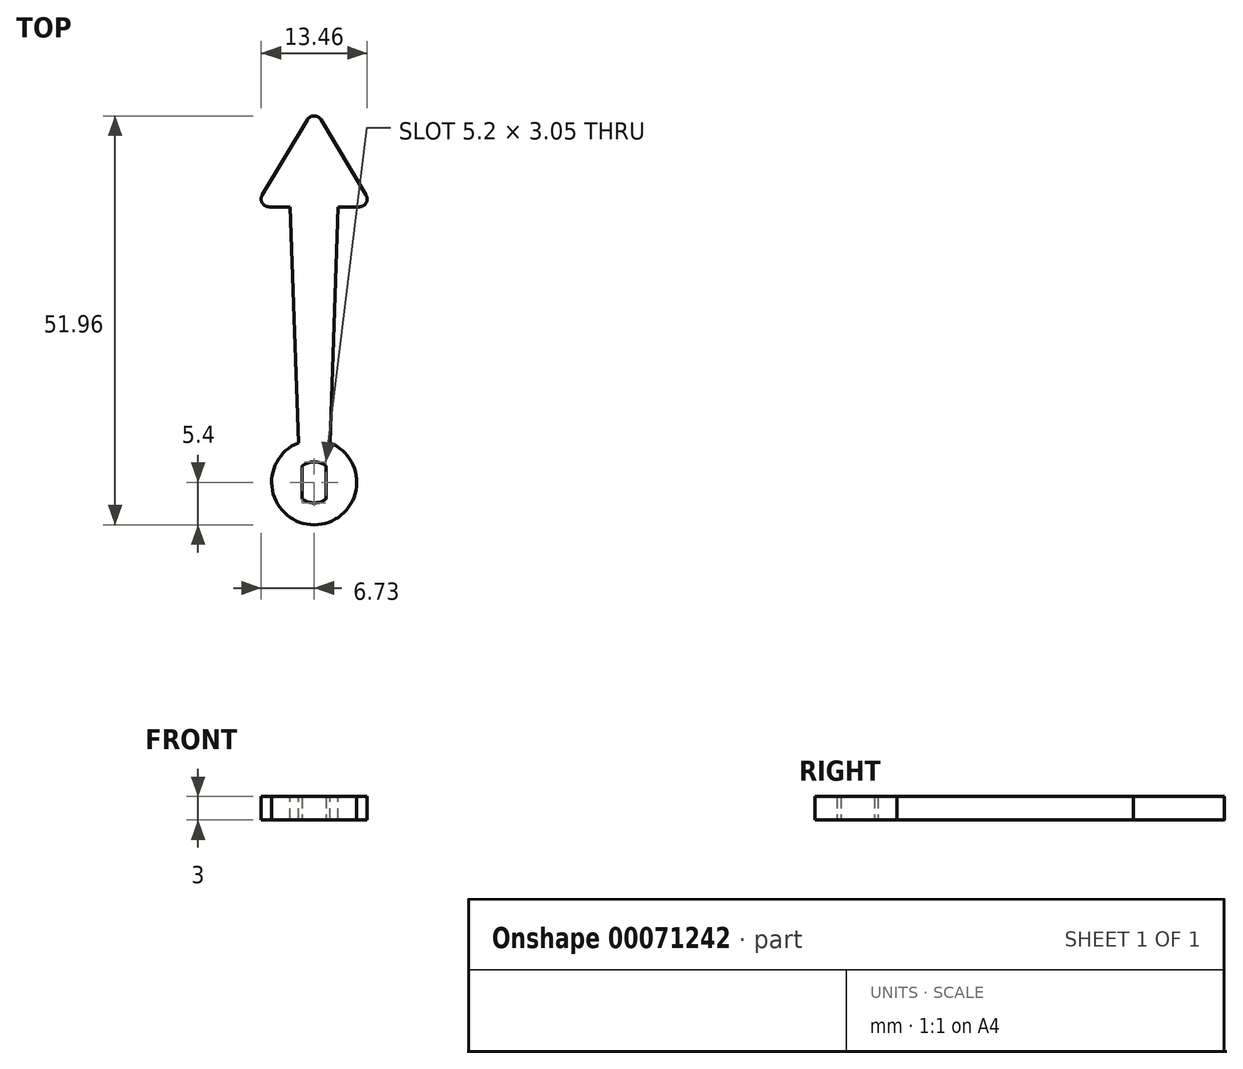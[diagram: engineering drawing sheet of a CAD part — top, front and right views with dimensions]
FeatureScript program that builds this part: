
annotation { "Feature Type Name" : "Feature", "Feature Type Description" : "" }
export const myFeature = defineFeature(function(context is Context, id is Id, definition is map)
    precondition{}
    {
        {
            var Q0;
            Q0=qCreatedBy(makeId("Top.planeOp"),FACE);
            var sketch = newSketch(context, id + "F0", { "sketchPlane" : qUnion([Q0])});
            skCircle(sketch, "E0", {"center": v(0, 0) * mm, "radius": 5.4 * mm});
            skCircle(sketch, "E1", {"center": v(0, 0) * mm, "radius": 2.6 * mm});
            skLineSegment(sketch, "E2", {"start": v(-1.52, 2.1) * mm, "end": v(-1.52, -2.1) * mm});
            skLineSegment(sketch, "E3", {"start": v(1.53, 2.1) * mm, "end": v(1.53, -2.1) * mm});
            skSolve(sketch);
        }
        {
            var Q0;
            Q0=makeQuery(id+"F0.imprint","IMPRINT",FACE,{"disambiguationData":[TD([[makeQuery(id+"F0.imprint","IMPRINT",EDGE,{"derivedFrom":sQuery(id+"F0.wireOp",EDGE,"E0")}),1.0]])]});
            var Q1;
            {var subQ0=sQuery(id+"F0.wireOp",EDGE,"E2");Q1=makeQuery(id+"F0.imprint","IMPRINT",FACE,{"disambiguationData":[TD([[makeQuery(id+"F0.imprint","IMPRINT",EDGE,{"derivedFrom":subQ0}),-1.0]])]});}
            var Q2;
            {var subQ0=sQuery(id+"F0.wireOp",EDGE,"E3");Q2=makeQuery(id+"F0.imprint","IMPRINT",FACE,{"disambiguationData":[TD([[makeQuery(id+"F0.imprint","IMPRINT",EDGE,{"derivedFrom":subQ0}),1.0]])]});}
            extrude(context, id + "F1", {"entities" : qUnion([Q0, Q1, Q2]), "endBound" : BoundingType.SYMMETRIC, "depth" : 3 * mm});
        }
        {
            var Q0;
            Q0=qCreatedBy(makeId("Top.planeOp"),FACE);
            var sketch = newSketch(context, id + "F2", { "sketchPlane" : qUnion([Q0])});
            skLineSegment(sketch, "E4", {"start": v(0, 0) * mm, "end": v(0, 35) * mm, "construction": true});
            skLineSegment(sketch, "E5", {"start": v(0, 35) * mm, "end": v(3.05, 35) * mm});
            skCircle(sketch, "E6.0.0", {"center": v(0, 0) * mm, "radius": 5.4 * mm});
            skLineSegment(sketch, "E7", {"start": v(3.05, 35) * mm, "end": v(2, 5.02) * mm});
            skLineSegment(sketch, "E8", {"start": v(0, 5.02) * mm, "end": v(2, 5.02) * mm});
            skLineSegment(sketch, "E9.MirrorCS", {"start": v(0, 5.02) * mm, "end": v(-2, 5.02) * mm});
            skLineSegment(sketch, "E10.MirrorCS", {"start": v(0, 35) * mm, "end": v(-3.05, 35) * mm});
            skLineSegment(sketch, "E11.MirrorCS", {"start": v(-3.05, 35) * mm, "end": v(-2, 5.02) * mm});
            skSolve(sketch);
        }
        {
            var Q0;
            Q0=makeQuery(id+"F2.imprint","IMPRINT",FACE,{"disambiguationData":[TD([[makeQuery(id+"F2.imprint","IMPRINT",EDGE,{"derivedFrom":sQuery(id+"F2.wireOp",EDGE,"E5")}),-1.0]])]});
            var Q1;
            Q1=makeQuery(id+"F1.opExtrude","CAP_FACE",FACE,{"disambiguationData":[OSD([sQuery(id+"F0.wireOp",EDGE,"E0"),sQuery(id+"F0.wireOp",EDGE,"E1"),sQuery(id+"F0.wireOp",EDGE,"E2"),sQuery(id+"F0.wireOp",EDGE,"E3")])],"isStart":true});
            extrude(context, id + "F3", {"entities" : qUnion([Q0]), "operationType" : NewBodyOperationType.ADD, "endBound" : BoundingType.SYMMETRIC, "oppositeDirection" : true, "endBoundEntityFace" : qUnion([Q1]), "depth" : 3 * mm});
        }
        {
            var Q0;
            Q0=makeQuery(id+"F3.boolean.opBoolean","MERGE",FACE,{"derivedFrom":[makeQuery(id+"F1.opExtrude","CAP_FACE",FACE,{"disambiguationData":[OSD([sQuery(id+"F0.wireOp",EDGE,"E0"),sQuery(id+"F0.wireOp",EDGE,"E1"),sQuery(id+"F0.wireOp",EDGE,"E2"),sQuery(id+"F0.wireOp",EDGE,"E3")])],"isStart":false}),makeQuery(id+"F3.opExtrude","CAP_FACE",FACE,{"disambiguationData":[OSD([sQuery(id+"F2.wireOp",EDGE,"E5"),sQuery(id+"F2.wireOp",EDGE,"E6.0.0"),sQuery(id+"F2.wireOp",EDGE,"E7"),sQuery(id+"F2.wireOp",EDGE,"E10.MirrorCS"),sQuery(id+"F2.wireOp",EDGE,"E11.MirrorCS")])],"isStart":true})]});
            var sketch = newSketch(context, id + "F4", { "sketchPlane" : qUnion([Q0])});
            skLineSegment(sketch, "E12", {"start": v(0, 35) * mm, "end": v(0, 47.5) * mm, "construction": true});
            skLineSegment(sketch, "E13", {"start": v(-7.5, 35) * mm, "end": v(7.5, 35) * mm});
            skLineSegment(sketch, "E14", {"start": v(0, 47.5) * mm, "end": v(-7.5, 35) * mm});
            skLineSegment(sketch, "E15", {"start": v(0, 47.5) * mm, "end": v(7.5, 35) * mm});
            skSolve(sketch);
        }
        {
            var Q0;
            Q0 = qSketchRegion(id + "F4", true);
            var Q1;
            Q1=makeQuery(id+"F3.boolean.opBoolean","MERGE",FACE,{"derivedFrom":[makeQuery(id+"F1.opExtrude","CAP_FACE",FACE,{"disambiguationData":[OSD([sQuery(id+"F0.wireOp",EDGE,"E0"),sQuery(id+"F0.wireOp",EDGE,"E1"),sQuery(id+"F0.wireOp",EDGE,"E2"),sQuery(id+"F0.wireOp",EDGE,"E3")])],"isStart":true}),makeQuery(id+"F3.opExtrude","CAP_FACE",FACE,{"disambiguationData":[OSD([sQuery(id+"F2.wireOp",EDGE,"E5"),sQuery(id+"F2.wireOp",EDGE,"E6.0.0"),sQuery(id+"F2.wireOp",EDGE,"E7"),sQuery(id+"F2.wireOp",EDGE,"E10.MirrorCS"),sQuery(id+"F2.wireOp",EDGE,"E11.MirrorCS")])],"isStart":false})]});
            extrude(context, id + "F5", {"entities" : qUnion([Q0]), "operationType" : NewBodyOperationType.ADD, "endBound" : BoundingType.UP_TO_SURFACE, "oppositeDirection" : true, "endBoundEntityFace" : qUnion([Q1]), "depth" : 25 * mm});
        }
        {
            var Q0;
            Q0=makeQuery(id+"F5.opExtrude","SWEPT_EDGE",EDGE,{"disambiguationData":[OSD([sQuery(id+"F4.wireOp",EDGE,"E13"),sQuery(id+"F4.wireOp",EDGE,"E14")])]});
            var Q1;
            Q1=makeQuery(id+"F5.opExtrude","SWEPT_EDGE",EDGE,{"disambiguationData":[OSD([sQuery(id+"F4.wireOp",EDGE,"E13"),sQuery(id+"F4.wireOp",EDGE,"E15")])]});
            var Q2;
            Q2=makeQuery(id+"F5.opExtrude","SWEPT_EDGE",EDGE,{"disambiguationData":[OSD([sQuery(id+"F4.wireOp",EDGE,"E14"),sQuery(id+"F4.wireOp",EDGE,"E15")])]});
            fillet(context, id + "F6", {"entities" : qUnion([Q0, Q1, Q2]), "radius" : 1 * mm, "tangentPropagation" : true, "allowEdgeOverflow" : false});
        }
    });
